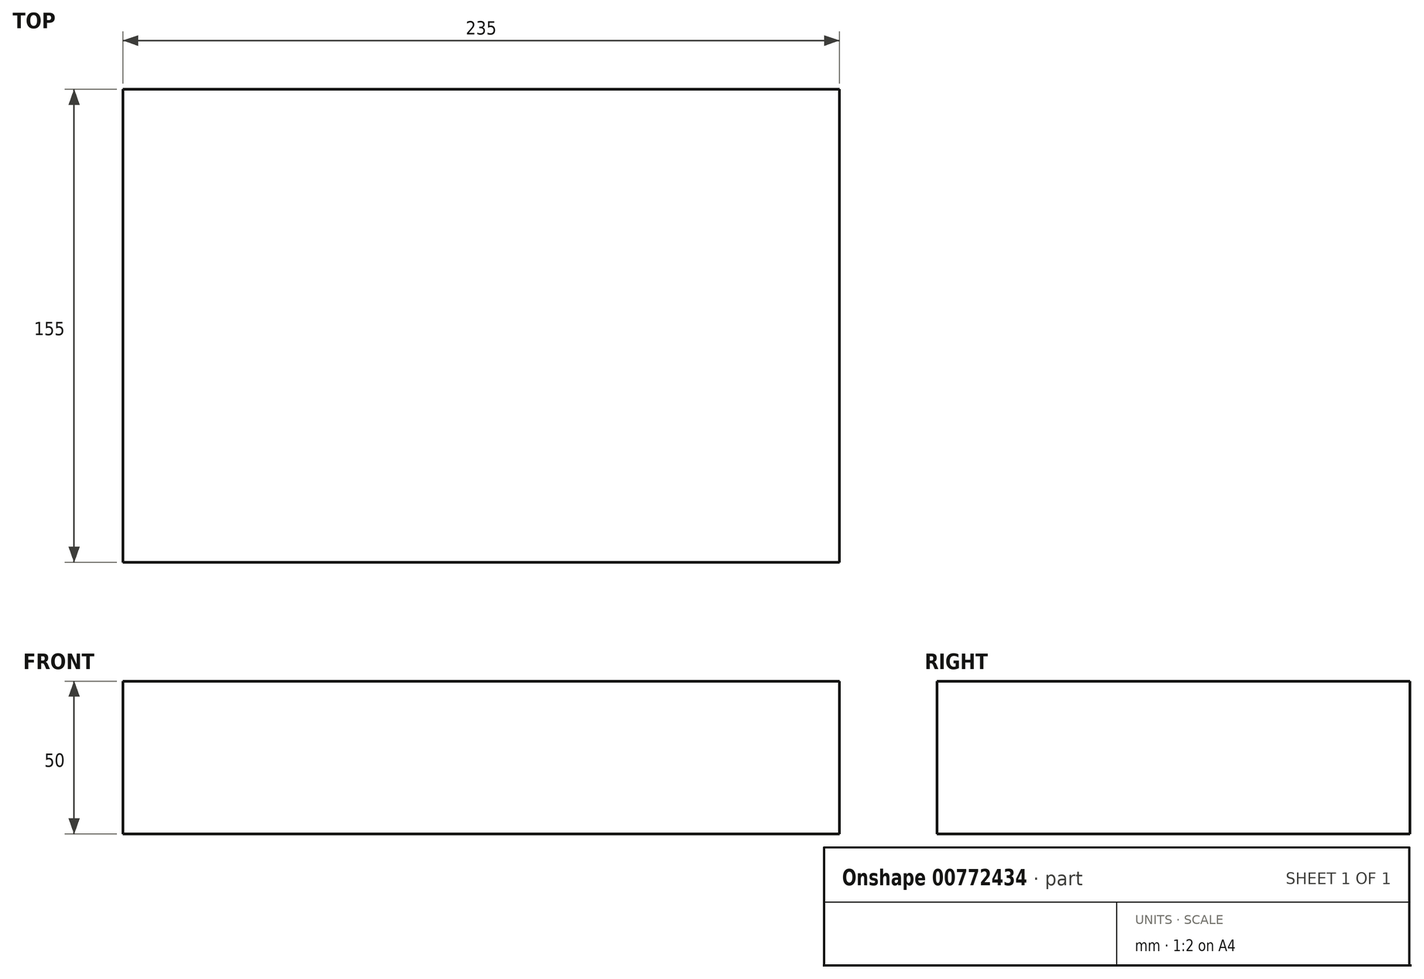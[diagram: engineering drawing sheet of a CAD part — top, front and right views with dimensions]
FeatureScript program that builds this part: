
annotation { "Feature Type Name" : "Feature", "Feature Type Description" : "" }
export const myFeature = defineFeature(function(context is Context, id is Id, definition is map)
    precondition{}
    {
        {
            var Q0;
            Q0=qCreatedBy(makeId("Top.planeOp"),FACE);
            var sketch = newSketch(context, id + "F0", { "sketchPlane" : qUnion([Q0])});
            skLineSegment(sketch, "E0.bottom", {"start": v(0, 0) * mm, "end": v(235, 0) * mm});
            skLineSegment(sketch, "E0.top", {"start": v(0, 155) * mm, "end": v(235, 155) * mm});
            skLineSegment(sketch, "E0.left", {"start": v(0, 0) * mm, "end": v(0, 155) * mm});
            skLineSegment(sketch, "E0.right", {"start": v(235, 0) * mm, "end": v(235, 155) * mm});
            skSolve(sketch);
        }
        {
            var Q0;
            Q0=makeQuery(id+"F0.imprint","IMPRINT",FACE,{"disambiguationData":[TD([[makeQuery(id+"F0.imprint","IMPRINT",EDGE,{"derivedFrom":sQuery(id+"F0.wireOp",EDGE,"E0.bottom")}),1.0]])]});
            extrude(context, id + "F1", {"entities" : qUnion([Q0]), "depth" : 50 * mm, "offsetDistance" : 25 * mm});
        }
    });
